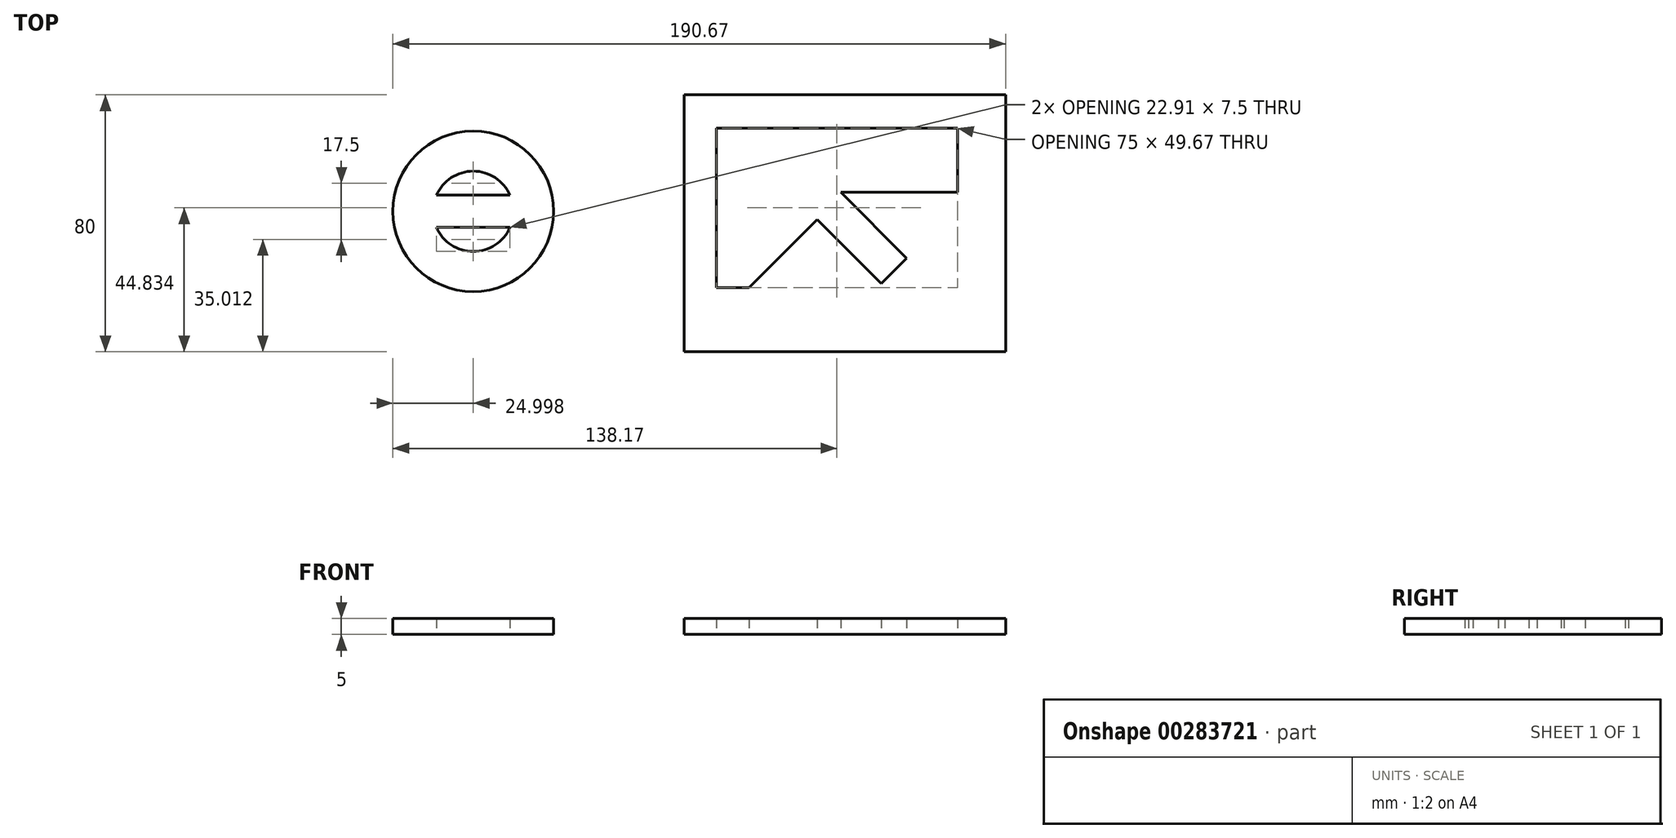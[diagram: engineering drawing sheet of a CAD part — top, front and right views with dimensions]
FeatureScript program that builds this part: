
annotation { "Feature Type Name" : "Feature", "Feature Type Description" : "" }
export const myFeature = defineFeature(function(context is Context, id is Id, definition is map)
    precondition{}
    {
        {
            var Q0;
            Q0=qCreatedBy(makeId("Top.planeOp"),FACE);
            var sketch = newSketch(context, id + "F0", { "sketchPlane" : qUnion([Q0])});
            skLineSegment(sketch, "E0.bottom", {"start": v(0, 0) * mm, "end": v(100, 0) * mm});
            skLineSegment(sketch, "E0.top", {"start": v(0, 80) * mm, "end": v(100, 80) * mm});
            skLineSegment(sketch, "E0.left", {"start": v(0, 0) * mm, "end": v(0, 80) * mm});
            skLineSegment(sketch, "E0.right", {"start": v(100, 0) * mm, "end": v(100, 80) * mm});
            skCircle(sketch, "E1", {"center": v(-65.67, 43.76) * mm, "radius": 25 * mm});
            skLineSegment(sketch, "E2", {"start": v(10, 20) * mm, "end": v(20.17, 20) * mm});
            skLineSegment(sketch, "E3", {"start": v(20.17, 20) * mm, "end": v(41.38, 41.21) * mm});
            skLineSegment(sketch, "E4", {"start": v(41.38, 41.21) * mm, "end": v(61.28, 21.3) * mm});
            skLineSegment(sketch, "E5", {"start": v(61.28, 21.3) * mm, "end": v(69.17, 29.2) * mm});
            skLineSegment(sketch, "E6", {"start": v(69.17, 29.2) * mm, "end": v(48.7, 49.67) * mm});
            skLineSegment(sketch, "E7", {"start": v(48.7, 49.67) * mm, "end": v(85, 49.67) * mm});
            skLineSegment(sketch, "E8", {"start": v(85, 49.67) * mm, "end": v(85, 69.67) * mm});
            skLineSegment(sketch, "E9", {"start": v(85, 69.67) * mm, "end": v(10, 69.67) * mm});
            skLineSegment(sketch, "E10", {"start": v(10, 69.67) * mm, "end": v(10, 20) * mm});
            skArc(sketch, "E11", {"start": v(-77.13, 38.76) * mm, "mid": v(-65.67, 31.26) * mm, "end": v(-54.22, 38.76) * mm});
            skLineSegment(sketch, "E12.bottom", {"start": v(-77.13, 48.76) * mm, "end": v(-54.22, 48.76) * mm});
            skLineSegment(sketch, "E12.top", {"start": v(-77.13, 38.76) * mm, "end": v(-54.22, 38.76) * mm});
            skArc(sketch, "E13.trimOffspring", {"start": v(-54.22, 48.76) * mm, "mid": v(-65.67, 56.26) * mm, "end": v(-77.13, 48.76) * mm});
            skSolve(sketch);
        }
        {
            var Q0;
            Q0=makeQuery(id+"F0.imprint","IMPRINT",FACE,{"disambiguationData":[TD([[makeQuery(id+"F0.imprint","IMPRINT",EDGE,{"derivedFrom":sQuery(id+"F0.wireOp",EDGE,"E1")}),1.0]])]});
            var Q1;
            Q1=makeQuery(id+"F0.imprint","IMPRINT",FACE,{"disambiguationData":[TD([[makeQuery(id+"F0.imprint","IMPRINT",EDGE,{"derivedFrom":sQuery(id+"F0.wireOp",EDGE,"E0.bottom")}),1.0]])]});
            extrude(context, id + "F1", {"entities" : qUnion([Q0, Q1]), "depth" : 5 * mm});
        }
    });
